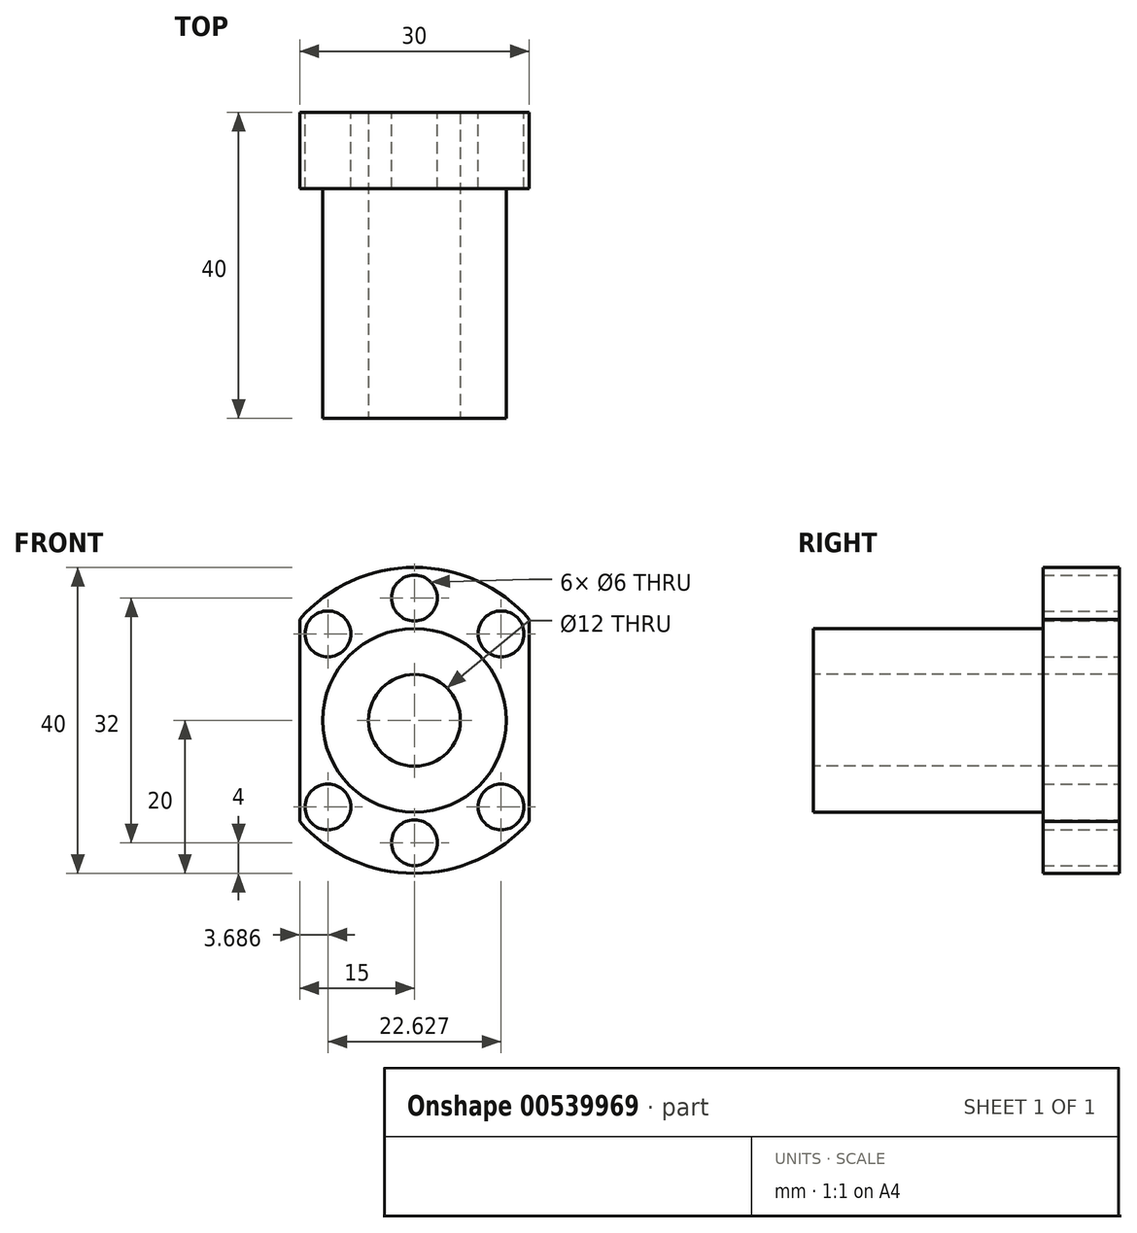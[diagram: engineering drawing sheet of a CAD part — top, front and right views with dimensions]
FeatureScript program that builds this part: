
annotation { "Feature Type Name" : "Feature", "Feature Type Description" : "" }
export const myFeature = defineFeature(function(context is Context, id is Id, definition is map)
    precondition{}
    {
        {
            var Q0;
            Q0=qCreatedBy(makeId("Front.planeOp"),FACE);
            var sketch = newSketch(context, id + "F0", { "sketchPlane" : qUnion([Q0])});
            skCircle(sketch, "E0", {"center": v(0, 0) * mm, "radius": 20 * mm});
            skSolve(sketch);
        }
        {
            var Q0;
            Q0=makeQuery(id+"F0.imprint","IMPRINT",FACE,{"disambiguationData":[TD([[makeQuery(id+"F0.imprint","IMPRINT",EDGE,{"derivedFrom":sQuery(id+"F0.wireOp",EDGE,"E0")}),1.0]])]});
            extrude(context, id + "F1", {"entities" : qUnion([Q0]), "depth" : 10 * mm, "offsetDistance" : 25 * mm});
        }
        {
            var Q0;
            Q0=makeQuery(id+"F1.opExtrude","CAP_FACE",FACE,{"disambiguationData":[OSD([sQuery(id+"F0.wireOp",EDGE,"E0")])],"isStart":false});
            var sketch = newSketch(context, id + "F2", { "sketchPlane" : qUnion([Q0])});
            skCircle(sketch, "E1", {"center": v(0, 0) * mm, "radius": 12 * mm});
            skSolve(sketch);
        }
        {
            var Q0;
            Q0=makeQuery(id+"F2.imprint","IMPRINT",FACE,{"disambiguationData":[TD([[makeQuery(id+"F2.imprint","IMPRINT",EDGE,{"derivedFrom":sQuery(id+"F2.wireOp",EDGE,"E1")}),1.0]])]});
            extrude(context, id + "F3", {"entities" : qUnion([Q0]), "operationType" : NewBodyOperationType.ADD, "depth" : 30 * mm, "offsetDistance" : 25 * mm});
        }
        {
            var Q0;
            Q0=makeQuery(id+"F3.opExtrude","CAP_FACE",FACE,{"disambiguationData":[OSD([sQuery(id+"F2.wireOp",EDGE,"E1")])],"isStart":false});
            var sketch = newSketch(context, id + "F4", { "sketchPlane" : qUnion([Q0])});
            skCircle(sketch, "E2", {"center": v(0, 0) * mm, "radius": 6 * mm});
            skSolve(sketch);
        }
        {
            var Q0;
            Q0=makeQuery(id+"F4.imprint","IMPRINT",FACE,{"disambiguationData":[TD([[makeQuery(id+"F4.imprint","IMPRINT",EDGE,{"derivedFrom":sQuery(id+"F4.wireOp",EDGE,"E2")}),1.0]])]});
            extrude(context, id + "F5", {"entities" : qUnion([Q0]), "operationType" : NewBodyOperationType.REMOVE, "endBound" : BoundingType.THROUGH_ALL, "oppositeDirection" : true, "depth" : 25 * mm, "offsetDistance" : 25 * mm});
        }
        {
            var Q0;
            Q0=makeQuery(id+"F1.opExtrude","CAP_FACE",FACE,{"disambiguationData":[OSD([sQuery(id+"F0.wireOp",EDGE,"E0")])],"isStart":true});
            var sketch = newSketch(context, id + "F6", { "sketchPlane" : qUnion([Q0])});
            skLineSegment(sketch, "E3.bottom", {"start": v(0, 0) * mm, "end": v(-15, 0) * mm, "construction": true});
            skLineSegment(sketch, "E3.top", {"start": v(0, 13.23) * mm, "end": v(-15, 13.23) * mm, "construction": true});
            skLineSegment(sketch, "E3.left", {"start": v(0, 0) * mm, "end": v(0, 13.23) * mm, "construction": true});
            skLineSegment(sketch, "E3.right", {"start": v(-15, 0) * mm, "end": v(-15, 13.23) * mm});
            skLineSegment(sketch, "E4.MirrorCS", {"start": v(0, 0) * mm, "end": v(0, -13.23) * mm, "construction": true});
            skLineSegment(sketch, "E5.MirrorCS", {"start": v(0, -13.23) * mm, "end": v(-15, -13.23) * mm, "construction": true});
            skLineSegment(sketch, "E6.MirrorCS", {"start": v(-15, 0) * mm, "end": v(-15, -13.23) * mm});
            skLineSegment(sketch, "E7.MirrorCS", {"start": v(15, 0) * mm, "end": v(15, 13.23) * mm});
            skLineSegment(sketch, "E8.MirrorCS", {"start": v(15, 0) * mm, "end": v(15, -13.23) * mm});
            skCircle(sketch, "E9.0", {"center": v(0, 0) * mm, "radius": 20 * mm});
            skSolve(sketch);
        }
        {
            var Q0;
            {var subQ0=sQuery(id+"F6.wireOp",EDGE,"E3.right");Q0=makeQuery(id+"F6.imprint","IMPRINT",FACE,{"disambiguationData":[TD([[makeQuery(id+"F6.imprint","IMPRINT",EDGE,{"derivedFrom":subQ0}),1.0]])]});}
            var Q1;
            {var subQ0=sQuery(id+"F6.wireOp",EDGE,"E7.MirrorCS");Q1=makeQuery(id+"F6.imprint","IMPRINT",FACE,{"disambiguationData":[TD([[makeQuery(id+"F6.imprint","IMPRINT",EDGE,{"derivedFrom":subQ0}),-1.0]])]});}
            extrude(context, id + "F7", {"entities" : qUnion([Q0, Q1]), "operationType" : NewBodyOperationType.REMOVE, "oppositeDirection" : true, "depth" : 25 * mm, "offsetDistance" : 25 * mm});
        }
        {
            var Q0;
            Q0=makeQuery(id+"F1.opExtrude","CAP_FACE",FACE,{"disambiguationData":[OSD([sQuery(id+"F0.wireOp",EDGE,"E0")])],"isStart":true});
            var sketch = newSketch(context, id + "F8", { "sketchPlane" : qUnion([Q0])});
            skCircle(sketch, "E10", {"center": v(0, 0) * mm, "radius": 16 * mm, "construction": true});
            skPoint(sketch, "E11", {"position": v(0, 16) * mm});
            skPoint(sketch, "E12.1.0", {"position": v(-11.31, 11.31) * mm});
            skPoint(sketch, "E12.2.0", {"position": v(-16, 0) * mm});
            skPoint(sketch, "E12.3.0", {"position": v(-11.31, -11.31) * mm});
            skPoint(sketch, "E12.4.0", {"position": v(0, -16) * mm});
            skPoint(sketch, "E12.5.0", {"position": v(11.31, -11.31) * mm});
            skPoint(sketch, "E12.6.0", {"position": v(16, 0) * mm});
            skPoint(sketch, "E12.7.0", {"position": v(11.31, 11.31) * mm});
            skSolve(sketch);
        }
        {
            var Q0;
            Q0=sQuery(id+"F8.wireOp",VERTEX,"E12.1.0");
            var Q1;
            Q1=sQuery(id+"F8.wireOp",VERTEX,"E11");
            var Q2;
            Q2=sQuery(id+"F8.wireOp",VERTEX,"E12.7.0");
            var Q3;
            Q3=sQuery(id+"F8.wireOp",VERTEX,"E12.3.0");
            var Q4;
            Q4=sQuery(id+"F8.wireOp",VERTEX,"E12.4.0");
            var Q5;
            Q5=sQuery(id+"F8.wireOp",VERTEX,"E12.5.0");
            var Q6;
            Q6=makeQuery(id+"F1.opExtrude","SWEPT_BODY",BODY,{"disambiguationData":[OSD([sQuery(id+"F0.wireOp",EDGE,"E0")])]});
            hole(context, id + "F9", {"style" : HoleStyle.SIMPLE, "endStyle" : HoleEndStyle.THROUGH, "holeDiameter" : 6 * mm, "majorDiameter" : 5 * mm, "isTappedThrough" : true, "tappedDepth" : 12 * mm, "tapClearance" : 3, "locations" : qUnion([Q0, Q1, Q2, Q3, Q4, Q5]), "scope" : qUnion([Q6])});
        }
    });
